# Revit family: QF_ELECTROLUXPROFESSIONAL_1L059Z_TD6-20_G
name_source: partatom
category: Attrezzature speciali
units: mm (PartAtom-declared; Revit-internal decimal feet)

## family parameters
Basato su piano di lavoro = No
Condiviso = No
Punto di calcolo locali = No
Quota connettore circolare = Usa diametro
Sempre verticale = Sì
Taglio con vuoti quando caricato = No
Tipo di parte = Normale

## types (41) — shared parameters
Depth Actual = 1202 mm  [stored 3.94357 ft]
Height Actual = 1771 mm  [stored 5.81037 ft]
Latent Heat Output = 0.0
Length Actual = 790 mm  [stored 2.59186 ft]
Modello = TD6-20
Produttore = Electrolux Professional
Sensible Heat Output = 0.0
URL = www.electroluxprofessional.com
Weight = 243
zero-valued in all types: Prospetto di default, Steam Pounds per Hour

## per-type parameters (varying)
| type | Cycle | Descrizione | Gas KW | Item Number | Phase | Volts | Watts |
| 9873830214 | 50 Hz | TUMBLE DRYER TD6-20 20KG SST DRUM GAS 21KW 400/50/3N COMPASS PRO 6L80 EU SILVER DO.RIGHT EXT.PM. DISCON. 2.I/O | 21 | 1LSPAE | 3 | 400 V | 1000 W |
| 9873830067 | 60 Hz | TUMBLE DRYER TD6-20 20KG GALVA.DRUM GAS 21KW 208-240/60/1 COMPASS PRO 6G82 EU SILVER DO.RIGHT STOP DISCON. EXT.CONN. | 21 | 1L0EHL | 1 | 240 V | 1200 W |
| 9873830032 | 50 Hz | TUMBLE DRYER TD6-20 20KG SST DRUM GAS 21KW 400/50/3 COMPASS PRO 6G81 EU SILVER DO.RIGHT MB STOP DISCON. | 21 | 1L0EDG | 3 | 400 V | 1000 W |
| 9873830022 | 60 Hz | TUMBLE DRYER TD6-20 20KG GALVA.DRUM GAS 21KW 240/60/3 COMPASS PRO 6G81 EU SILVER DO.RIGHT MB STOP DISCON. | 21 | 1LSN2R | 3 | 240 V | 1000 W |
| 9873830227 | 50 Hz | TUMBLE DRYER TD6-20 20KG GALVA.DRUM GAS 21KW 240/50/1N COMPASS PRO 6L80 EU SILVER DO.RIGHT EXT.PM. 2.I/O | 21 | 1L0GNG | 1 | 240 V | 1200 W |
| 9873830110 | 50 Hz | TUMBLE DRYER TD6-20 20KG GALVA.DRUM GAS 21KW 400/50/3N COMPASS PRO 6G81 EU SILVER DO.RIGHT MB STOP DISCON. | 21 | 1LSN52 | 3 | 400 V | 1000 W |
| 9873830100 | 50 Hz | TUMBLE DRYER TD6-20 20KG GALVA.DRUM GAS 21KW 230/50/1N COMPASS PRO 6G81 EU SILVER DO.RIGHT MB STOP DISCON. | 21 | 1L0EJG | 1 | 230 V | 1200 W |
| 9873830128 | 60 Hz | TUMBLE DRYER TD6-20 20KG SST DRUM GAS 21KW 380-415/60/3 COMPASS PRO 6G81 EU SST DO.LEFT MB STOP DISCON. | 21 | 1LSN8P | 3 | 415 V | 1000 W |
| 9873830190 | 60 Hz | TUMBLE DRYER TD6-20 20KG GALVA.DRUM GAS 21KW 240/60/1N COMPASS PRO 6G82 EU SILVER DO.RIGHT STOP DISCON. | 21 | 1LSNVC | 1 | 240 V | 1200 W |
| 9873830178 | 50 Hz | TUMBLE DRYER TD6-20 20KG GALVA.DRUM GAS 21KW 400/50/3 COMPASS PRO 6L80 EU SILVER DO.RIGHT | 21 | 1LSNSH | 3 | 400 V | 1000 W |
| 9873830071 | 60 Hz | TUMBLE DRYER TD6-20 20KG GALVA.DRUM GAS 21KW 208-240/60/1 COMPASS PRO 6G81 EU SILVER DO.RIGHT MB STOP DISCON. EXT.CONN. | 21 | 1L0EHR | 1 | 240 V | 1200 W |
| 9873830091 | 50 Hz | TUMBLE DRYER TD6-20 20KG GALVA.DRUM GAS 21KW 380-415/50/3 COMPASS PRO 6L80 EU SILVER DO.RIGHT EXT.PM. DISCON. 2.I/O | 21 | 1L80E6 | 3 | 415 V | 1000 W |
| 9873830125 | 50 Hz | TUMBLE DRYER TD6-20 20KG GALVA.DRUM GAS 21KW 230/50/1N COMPASS PRO 6L80 EU SILVER DO.RIGHT EXT.PM. DISCON. 2.I/O | 21 | 1LSN8H | 1 | 230 V | 1200 W |
| 9873830175 | 50 Hz | TUMBLE DRYER TD6-20 20KG GALVA.DRUM GAS 21KW 230/50/1N COMPASS PRO 6L80 EU SILVER DO.LEFT | 21 | 1LSNSE | 1 | 230 V | 1200 W |
| 9873830099 | 50 Hz | TUMBLE DRYER TD6-20 20KG GALVA.DRUM GAS 21KW 400/50/3 COMPASS PRO 6G81 EU SILVER DO.RIGHT MB STOP DISCON. | 21 | 1L0EJ1 | 3 | 400 V | 1000 W |
| 9873830122 | 60 Hz | TUMBLE DRYER TD6-20 20KG GALVA.DRUM GAS 21KW 208-240/60/3 COMPASS PRO 6L80 EU SILVER DO.LEFT | 21 | 1L0EL1 | 3 | 240 V | 1000 W |
| 9873830102 | 60 Hz | TUMBLE DRYER TD6-20 20KG SST DRUM GAS 21KW 380-415/60/3 COMPASS PRO 6G81 EU SST DO.RIGHT.INS. MB STOP DISCON. EXT.CONN. | 21 | 1L0EJJ | 3 | 415 V | 1000 W |
| 9873830235 | 60 Hz | TUMBLE DRYER TD6-20 20KG SST DRUM GAS 21KW 220/60/3 COMPASS PRO 6G82 EU SILVER DO.RIGHT STOP DISCON. | 21 | 1L0GVX | 3 | 220 V | 1000 W |
| 9873830172 | 50 Hz | TUMBLE DRYER TD6-20 20KG GALVA.DRUM GAS 21KW 230/50/3 COMPASS PRO 6G81 EU SILVER DO.RIGHT MB STOP DISCON. | 21 | 1LSNPT | 3 | 230 V | 1000 W |
| 9873830215 | 50 Hz | TUMBLE DRYER TD6-20 20KG SST DRUM GAS 21KW 400/50/3N COMPASS PRO 6G82 EU SILVER DO.RIGHT STOP DISCON. | 21 | 1LSPAF | 3 | 400 V | 1000 W |
| 9873830033 | 50 Hz | TUMBLE DRYER TD6-20 20KG SST DRUM GAS 21KW 400/50/3 COMPASS PRO 6G82 EU SILVER DO.RIGHT STOP DISCON. | 21 | 1L0EDH | 3 | 400 V | 1000 W |
| 9873830192 | 60 Hz | TUMBLE DRYER TD6-20 20KG GALVA.DRUM GAS 21KW 208-240/60/3 COMPASS PRO 6G82 EU SILVER DO.RIGHT STOP DISCON. EXT.CONN. | 21 | 1LSNYA | 3 | 240 V | 1000 W |
| 9873830200 | 50 Hz | TUMBLE DRYER TD6-20 20KG GALVA.DRUM GAS 21KW 230/50/1N COMPASS PRO 6G81 EU SILVER DO.LEFT MB STOP DISCON. | 21 | 1LA0AG | 1 | 230 V | 1200 W |
| 9873830270 | 50 Hz | TUMBLE DRYER TD6-20 20KG SST DRUM GPL 21KW 200/50/3 COMPASS PRO 6G86 JP SILVER DO.RIGHT DISCON. | 0 | 1LT5ZF | 3 | 200 V | 1000 W |
| 9873830290 | 60 Hz | TUMBLE DRYER TD6-20 20KG SST DRUM GPL 21KW 200/60/3 COMPASS PRO 6L85 JP SILVER DO.RIGHT DISCON. EXT.CONN. | 0 | 1L0HAC | 3 | 200 V | 1000 W |
| 9873830177 | 50 Hz | TUMBLE DRYER TD6-20 20KG SST DRUM GAS 21KW 230/50/1N COMPASS PRO 6L80 EU SILVER DO.RIGHT | 21 | 1LSNSG | 1 | 230 V | 1200 W |
| 9873830302 | 50 Hz | TUMBLE DRYER TD6-20 20KG SST DRUM GAS 21KW 400/50/3 COMPASS PRO 6G81 EU SILVER DO.RIGHT MB DSC STOP DISCON. | 0 | 1LT6HY | 3 | 400 V | 1000 W |
| 9873830187 | 60 Hz | TUMBLE DRYER TD6-20 20KG GALVA.DRUM GAS 21KW 240/60/1N COMPASS PRO 6G81 EU SILVER DO.RIGHT MB STOP DISCON. | 21 | 1LSNV9 | 1 | 240 V | 1200 W |
| 9873830288 | 60 Hz | TUMBLE DRYER TD6-20 20KG SST DRUM GAS 21KW 208-240/60/1 COMPASS PRO 6G81 EU SST DO.LEFT MB STOP DISCON. | 0 | 1L0H9R | 1 | 240 V | 1000 W |
| 9873830213 | 50 Hz | TUMBLE DRYER TD6-20 20KG GALVA.DRUM GAS 21KW 380-415/50/3N COMPASS PRO 6L80 EU SILVER DO.RIGHT EXT.PM. DISCON. 2.I/O | 21 | 1LSPAD | 3 | 415 V | 1000 W |
| 9873830066 | 50 Hz | TUMBLE DRYER TD6-20 20KG SST DRUM GAS 21KW 400/50/3 COMPASS PRO 6L80 EU SILVER DO.RIGHT EXT.PM. DISCON. 2.I/O | 21 | 1L0EHK | 3 | 400 V | 1000 W |
| 9873830273 | 60 Hz | TUMBLE DRYER TD6-20 20KG SST DRUM GPL 21KW 200/60/3 COMPASS PRO 6G86 JP SILVER DO.RIGHT DISCON. | 0 | 1LT5ZJ | 3 | 200 V | 1000 W |
| 9873830293 | 50 Hz | TUMBLE DRYER TD6-20 20KG GALVA.DRUM GAS 21KW 230/50/1N COMPASS PRO 6L80 EU SILVER DO.RIGHT | 0 | 1LM09V | 1 | 230 V | 1000 W |
| 9873830114 | 50 Hz | TUMBLE DRYER TD6-20 20KG GALVA.DRUM GAS 21KW 400/50/3N COMPASS PRO 6G81 EU SILVER DO.RIGHT.INS. MB STOP DISCON. | 21 | 1LSN62 | 3 | 400 V | 1000 W |
| 9873830121 | 60 Hz | TUMBLE DRYER TD6-20 20KG GALVA.DRUM GAS 21KW 208-240/60/1 COMPASS PRO 6L80 EU SILVER DO.LEFT | 21 | 1L0EL0 | 1 | 240 V | 1200 W |
| 9873830216 | 50 Hz | TUMBLE DRYER TD6-20 20KG SST DRUM GAS 21KW 400/50/3N COMPASS PRO 6G81 EU SILVER DO.RIGHT MB STOP DISCON. | 21 | 1LSPAG | 3 | 400 V | 1000 W |
| 9873830101 | 50 Hz | TUMBLE DRYER TD6-20 20KG GALVA.DRUM GAS 21KW 230/50/1N COMPASS PRO 6G82 EU SILVER DO.RIGHT STOP DISCON. | 21 | 1L0EJH | 1 | 230 V | 1200 W |
| 9873830119 | 50 Hz | TUMBLE DRYER TD6-20 20KG GALVA.DRUM GAS 21KW 380-415/50/3N COMPASS PRO 6G82 EU SILVER DO.LEFT STOP DISCON. | 21 | 1L8219 | 3 | 415 V | 1000 W |
| 9873830070 | 60 Hz | TUMBLE DRYER TD6-20 20KG SST DRUM GAS 21KW 208-240/60/1 COMPASS PRO 6G82 EU SST DO.RIGHT.INS. STOP DISCON. EXT.CONN. | 21 | 1L0EHP | 1 | 240 V | 1200 W |
| 9873830259 | 60 Hz | TUMBLE DRYER TD6-20 20KG SST DRUM GAS 21KW 380-415/60/3 COMPASS PRO 6G82 EU SST DO.RIGHT DSC STOP DISCON. | 21 | 1L0H1W | 3 | 415 V | 1000 W |
| 9873830289 | 50 Hz | TUMBLE DRYER TD6-20 20KG SST DRUM GPL 21KW 200/50/3 COMPASS PRO 6L85 JP SILVER DO.RIGHT DISCON. EXT.CONN. | 0 | 1L0HAB | 3 | 200 V | 1000 W |

note: [stored X ft] marks values corroborated as IEEE doubles in the binary element streams (Revit-internal decimal feet)

## geometry (parser evidence)
native form markers: Blend x6
no freeform markers — native parametric forms only
